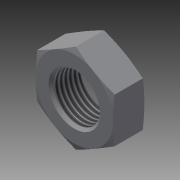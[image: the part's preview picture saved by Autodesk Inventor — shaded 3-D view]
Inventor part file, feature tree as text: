
AUTODESK INVENTOR PART (.ipt)
format: ipt  version: 2014 SP2 (Build 180246200, 246)  size: 157,184 bytes
history: native  units: in
note: dims shown in document units (in); Inventor stores cm internally (conversion verified against a paired STEP export)
features: other x70, sketch x3, revolve x2, extrude x1, thread x1
ambient origin geometry x8: Origin, YZ Plane, XZ Plane, XY Plane, X Axis, Y Axis, Z Axis, Center Point
bodies: Solid1 (feature_tree)
feature tree (77):
  sketch  "Sketch_8"  dims[d0=360.0deg d1=0.38in d2=0.0in]
  sketch  "Sketch_10"  dims[d3=360.0deg d4=0.3199in d5=0.0in]
  revolve  "Revolution1"  [1 undecoded]
  extrude  "Extrusion1"  Depth=0.3199in TaperAngle=0.0deg
  revolve  "Revolution2"  [1 undecoded]
  thread  "Thread1"  [1 undecoded]
  other  "NUT_XY"
  other  "NUT_YZ"
  other  "NUT_ZX"
  other  "NUT_X"
  other  "NUT_Y"
  other  "NUT_Z"
  other  "NUT_Center"
  other  "a1_XY"
  other  "a1_YZ"
  other  "a1_ZX"
  other  "a1_X"
  other  "a1_Y"
  other  "a1_Z"
  other  "a1_Center"
  other  "a2_XY"
  other  "a2_YZ"
  other  "a2_ZX"
  other  "a2_X"
  other  "a2_Y"
  other  "a2_Z"
  other  "a2_Center"
  other  "b1_XY"
  other  "b1_YZ"
  other  "b1_ZX"
  other  "b1_X"
  other  "b1_Y"
  other  "b1_Z"
  other  "b1_Center"
  other  "b2_XY"
  other  "b2_YZ"
  other  "b2_ZX"
  other  "b2_X"
  other  "b2_Y"
  other  "b2_Z"
  other  "b2_Center"
  other  "e_XY"
  other  "e_YZ"
  other  "e_ZX"
  other  "e_X"
  other  "e_Y"
  other  "e_Z"
  other  "e_Center"
  other  "ol1_XY"
  other  "ol1_YZ"
  other  "ol1_ZX"
  other  "ol1_X"
  other  "ol1_Y"
  other  "ol1_Z"
  other  "ol1_Center"
  other  "ol2_XY"
  other  "ol2_YZ"
  other  "ol2_ZX"
  other  "ol2_X"
  other  "ol2_Y"
  other  "ol2_Z"
  other  "ol2_Center"
  other  "th1_XY"
  other  "th1_YZ"
  other  "th1_ZX"
  other  "th1_X"
  other  "th1_Y"
  other  "th1_Z"
  other  "th1_Center"
  other  "th2_XY"
  other  "th2_YZ"
  other  "th2_ZX"
  other  "th2_X"
  other  "th2_Y"
  other  "th2_Z"
  other  "th2_Center"
  sketch  "Sketch_11"  dims[d6=0.0in d7=0.0in d8=0.0in]
note: 3 required parameter values undecoded (feature->parameter linkage not recoverable at this tier; creation-order binding heuristic only, values carry confidence <= 0.55)